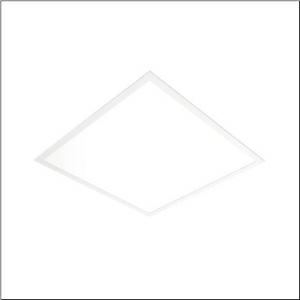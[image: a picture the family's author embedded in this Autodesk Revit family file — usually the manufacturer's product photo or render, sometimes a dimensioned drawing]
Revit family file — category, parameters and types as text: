
# Revit family: apollon_r__41_51mh11wd2443_7c66
name_source: partatom
category: Lighting Fixtures
units: mm (PartAtom-declared; Revit-internal decimal feet)

## family parameters
Cut with Voids When Loaded = No
Host = Face
Light Source = No
Part Type = Normal
Room Calculation Point = No
Round Connector Dimension = Use Diameter
Shared = No

## types (1)
- Apollon® 41 (1 x LED, 3500 lm, 28.5 W, 4000K)
    Apparent Load = 29 VA
    CIE Flux Codes = 61 87 97 100 100
    Color Rendering = 80
    Color Temperature = 4000K
    Default Elevation = 1800 mm
    Description = Apollon® 41, office luminaire, primary optical cover: prismatic diffuser, of PS, light emission: direct distribution, primary light characteristic: symmetric, installation type: lay-in mounting, LED, rated luminous flux: 3.500lm, luminous efficacy: 123lm/W, light colour: 840, colour temperature: 4000K, control gear: DALI 2, with terminal, 5-pole, mains connection: 220..240V, AC, 50/60Hz, housing, of aluminium section, traffic white (RAL 9016), module: M625, length: 620mm, width: 620mm, height: 60mm, recess depth: 180mm, housing upper side, of sheet steel, protection rating (complete): IP20, protection rating (lamp compartment, on room side): IP40, insulation class (complete): insulation class II (safety insulation), certification: CE, ENEC, impact resistance: IK03, permissible operating ambient temperature: -25..+40°C, packaging unit: 1 piece
    Height = 0 mm  [stored 0 ft]
    Lamp = 1 x LED
    Lamp Light Flux = 3500 lm
    Lamp Power = 28.5 W
    Lamp count = 1
    Length = 620 mm
    Luminous efficacy = 123 lm/W
    Manufacturer = Siteco
    ModVariant = No
    Model = 51MH11WD2443
    Mounting Place = Ceiling
    Mounting Type = Recessed
    Number of Poles = 1
    OnlyDefault = Yes
    Power Factor = 1
    Product Name = Apollon® 41
    Product group = office luminaire | ceiling recessed
    ProductGroupID = 401
    Protection Class = Protection class II
    Protection Degree = IP 20
    RLX_Detail_Level = 1
    RLX_Emergency_Light_Flux = 0 lm
    RLX_Emergency_Type = 0
    RLX_Emergency_Type_DB = No
    RlxData = <blob elided: 12261 chars, md5=35eaf58a>
    Socket = socket
    Standby Power = 0 W
    System Light Flux = 3500 lm
    System Power = 29 W
    Type Comments = Product without accessories
    Type Image = l_1291024.jpg
    URL = http://relux.com
    VarID = ---
    Voltage = 0 V
    Weight = 0.00 kg
    Width = 620 mm

note: [stored X ft] marks values corroborated as IEEE doubles in the binary element streams (Revit-internal decimal feet)

## geometry (parser evidence)
native form markers: Sweep x8
no freeform markers — native parametric forms only
